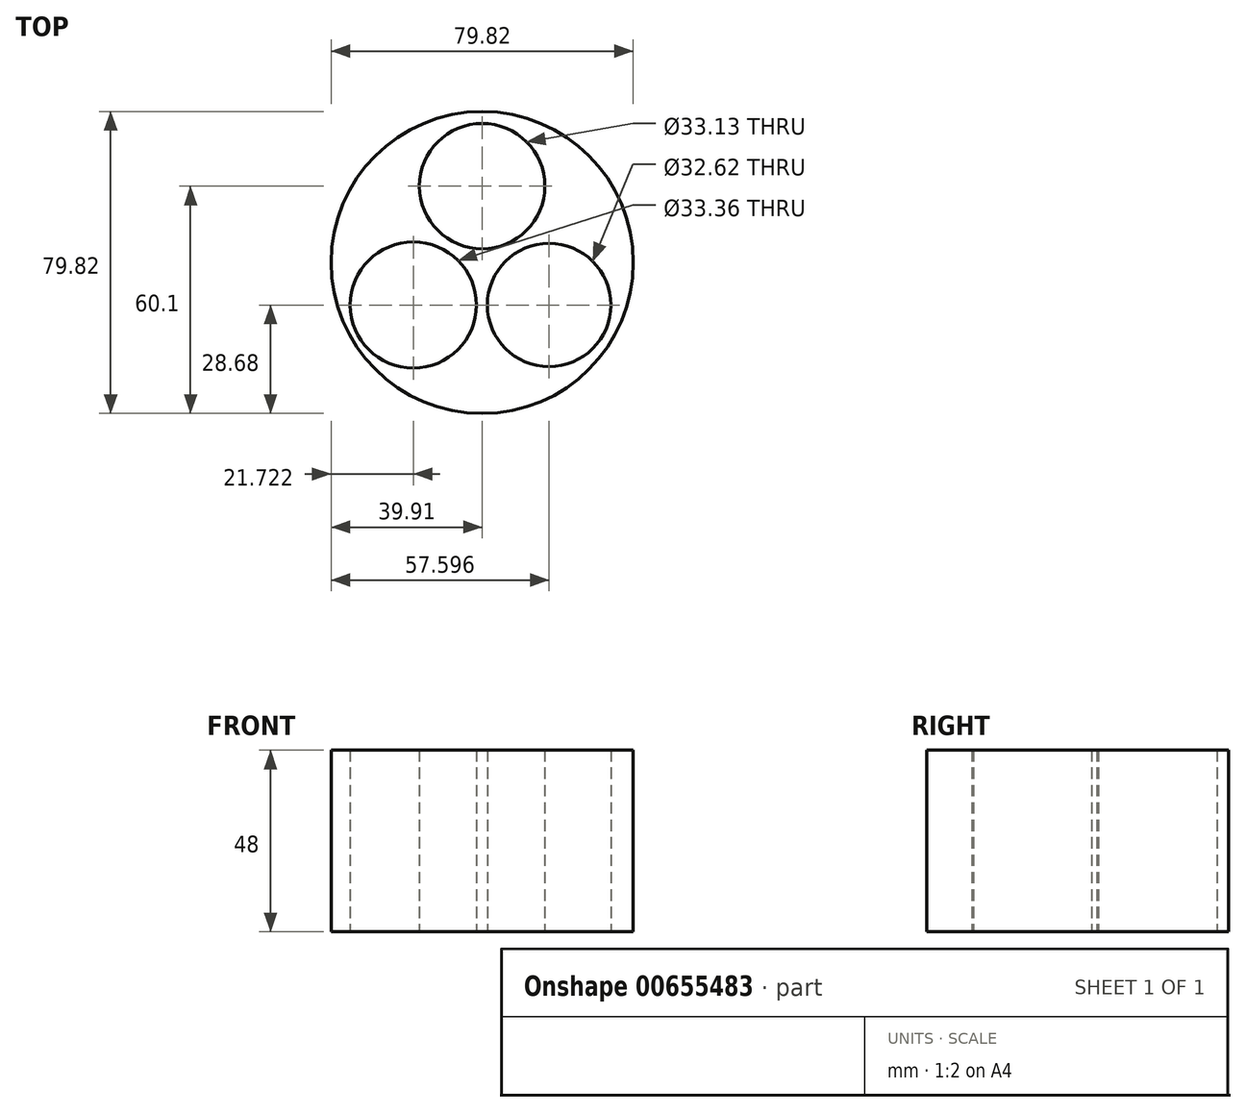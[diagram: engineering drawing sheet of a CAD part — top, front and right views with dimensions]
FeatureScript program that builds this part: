
annotation { "Feature Type Name" : "Feature", "Feature Type Description" : "" }
export const myFeature = defineFeature(function(context is Context, id is Id, definition is map)
    precondition{}
    {
        {
            var Q0;
            Q0=qCreatedBy(makeId("Top.planeOp"),FACE);
            var sketch = newSketch(context, id + "F0", { "sketchPlane" : qUnion([Q0])});
            skCircle(sketch, "E0", {"center": v(0, 0) * mm, "radius": 39.91 * mm});
            skCircle(sketch, "E1", {"center": v(0, 20.2) * mm, "radius": 16.57 * mm});
            skCircle(sketch, "E2", {"center": v(17.69, -11.23) * mm, "radius": 16.3 * mm});
            skCircle(sketch, "E3", {"center": v(-18.19, -11.23) * mm, "radius": 16.68 * mm});
            skSolve(sketch);
        }
        {
            var Q0;
            Q0=makeQuery(id+"F0.imprint","IMPRINT",FACE,{"disambiguationData":[TD([[makeQuery(id+"F0.imprint","IMPRINT",EDGE,{"derivedFrom":sQuery(id+"F0.wireOp",EDGE,"E0")}),1.0]])]});
            extrude(context, id + "F1", {"entities" : qUnion([Q0]), "depth" : 48 * mm, "offsetDistance" : 25 * mm});
        }
    });
